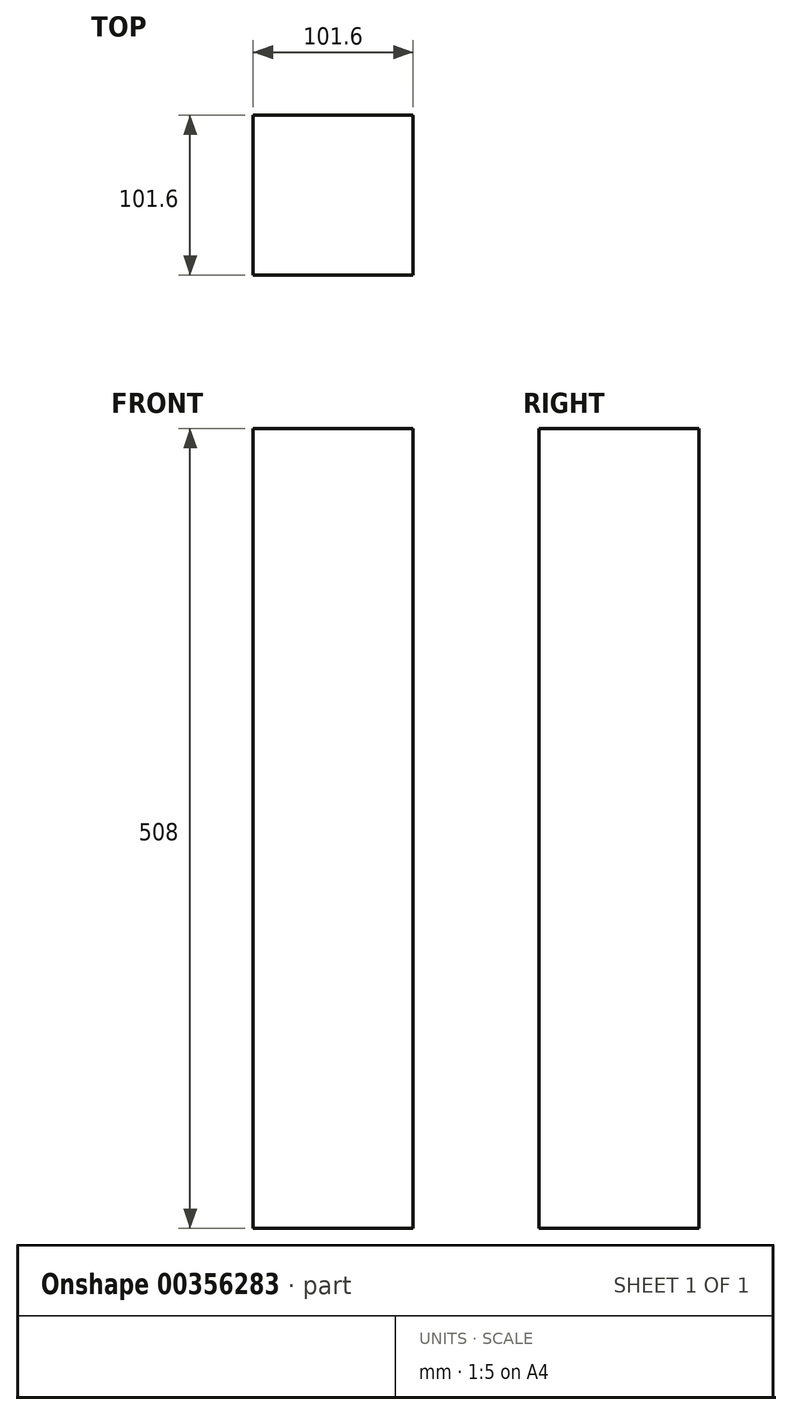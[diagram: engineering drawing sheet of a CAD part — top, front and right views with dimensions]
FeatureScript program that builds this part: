
annotation { "Feature Type Name" : "Feature", "Feature Type Description" : "" }
export const myFeature = defineFeature(function(context is Context, id is Id, definition is map)
    precondition{}
    {
        {
            var Q0;
            Q0=qCreatedBy(makeId("Front.planeOp"),FACE);
            var sketch = newSketch(context, id + "F0", { "sketchPlane" : qUnion([Q0])});
            skLineSegment(sketch, "E0.bottom", {"start": v(-113.98, 196.34) * mm, "end": v(-12.38, 196.34) * mm});
            skLineSegment(sketch, "E0.top", {"start": v(-113.98, -311.66) * mm, "end": v(-12.38, -311.66) * mm});
            skLineSegment(sketch, "E0.left", {"start": v(-113.98, 196.34) * mm, "end": v(-113.98, -311.66) * mm});
            skLineSegment(sketch, "E0.right", {"start": v(-12.38, 196.34) * mm, "end": v(-12.38, -311.66) * mm});
            skSolve(sketch);
        }
        {
            var Q0;
            Q0=makeQuery(id+"F0.imprint","IMPRINT",FACE,{"disambiguationData":[TD([[makeQuery(id+"F0.imprint","IMPRINT",EDGE,{"derivedFrom":sQuery(id+"F0.wireOp",EDGE,"E0.bottom")}),-1.0]])]});
            extrude(context, id + "F1", {"entities" : qUnion([Q0]), "depth" : 101.6 * mm});
        }
    });
